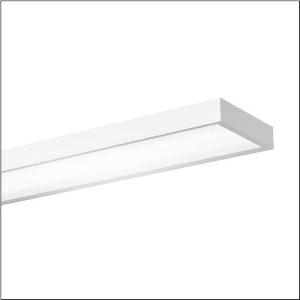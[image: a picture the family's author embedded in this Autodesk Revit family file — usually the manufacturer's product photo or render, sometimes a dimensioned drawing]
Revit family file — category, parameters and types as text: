
# Revit family: sport_31_51hs12dd4jca
name_source: partatom
category: Lighting Fixtures
units: mm (PartAtom-declared; Revit-internal decimal feet)

## family parameters
Cut with Voids When Loaded = No
Host = Face
Light Source = No
Part Type = Normal
Room Calculation Point = No
Round Connector Dimension = Use Diameter
Shared = No

## types (1)
- --- (1 x LED, 19720 lm, 146.2 W, 4000K)
    Apparent Load = 146 VA
    CIE Flux Codes = 65 89 97 100 100
    Color Rendering = 80
    Color Temperature = 4000K
    Default Elevation = 1800 mm
    Description = Sport 31, LED high bay luminaire, primary light control with reflector, of sheet steel, primary anti-glare with prismatic structure, of PC, primary optical cover: cover panel, of PC, light emission: direct distribution, primary light characteristic: symmetric, installation type: suspended mounting, recessed, surface-mounted, LED, rated luminous flux: 20.000lm, luminous efficacy: 137lm/W, light colour: 840, colour temperature: 4000K, control gear: ECG DALI, with terminal, 5-pole, max. 2.5mm², mains connection: 220..240V, AC/DC, 50/60Hz, rated input power: 146W, housing, of sheet steel, traffic white (RAL 9016), length: 1.540mm, width: 415mm, height: 95mm, protection rating (complete): IP20, protection rating (lamp compartment, on room side): IP50, insulation class (complete): insulation class I (protective earthing), certification: CE, ENEC, UKCA, ball protection: ball impact resistant with ceiling mounting or chain suspension, impact resistance: IK08, permissible operating ambient temperature: -20..+35°C, standard: DIN 18032-3, EN 60598-2-22, packaging unit: 1 piece
    Height = 100 mm  [stored 0.328084 ft]
    Lamp = 1 x LED
    Lamp Light Flux = 19720 lm
    Lamp Power = 146.2 W
    Lamp count = 1
    Length = 1500 mm
    Luminous efficacy = 135 lm/W
    Manufacturer = Siteco
    ModVariant = No
    Model = 51HS12DD4JCA
    Mounting Place = Ceiling
    Mounting Type = Pendant
    Number of Poles = 1
    OnlyDefault = Yes
    Power Factor = 1
    Product Name = Sport 31
    Product group = LED high bay luminaire
    ProductGroupID = 903
    Protection Class = Protection class I
    Protection Degree = IP 20
    RLX_Detail_Level = 1
    RLX_Emergency_Light_Flux = 0 lm
    RLX_Emergency_Type = 0
    RLX_Emergency_Type_DB = No
    RlxData = <blob elided: 24081 chars, md5=c8ae2d16>
    Socket = socket
    Standby Power = 0 W
    System Light Flux = 19719 lm
    System Power = 146 W
    Type Comments = factory setting: luminous flux: 100 % | dim-lin: 254 | 610 mA
    Type Image = l_1006829.jpg
    URL = http://relux.com
    VarID = @adj_132969
    Voltage = 0 V
    Weight = 0.00 kg
    Width = 415 mm

note: [stored X ft] marks values corroborated as IEEE doubles in the binary element streams (Revit-internal decimal feet)

## geometry (parser evidence)
native form markers: Blend x4, Sweep x10
no freeform markers — native parametric forms only
